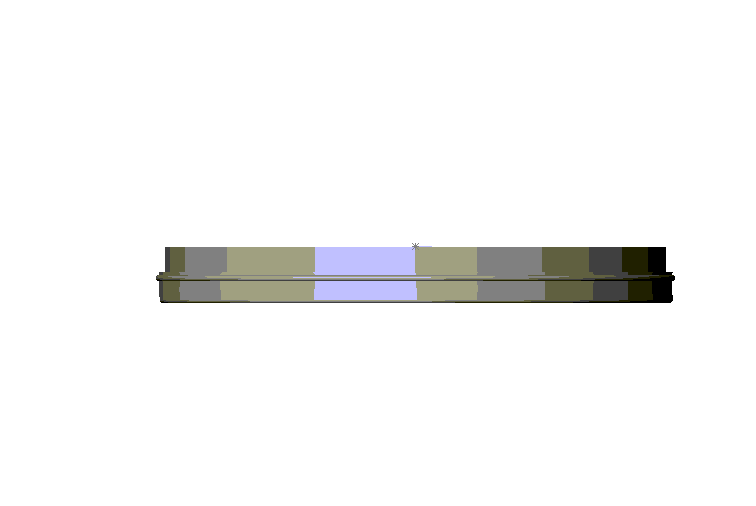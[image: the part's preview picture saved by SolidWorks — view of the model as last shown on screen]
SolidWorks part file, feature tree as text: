
SOLIDWORKS PART (.sldprt)
format: sldprt  version: not decoded by parser v0  size: 181,760 bytes
history: native  units: mm
features: sketch x6, cut_extrude x4, plane x3, extrude x1, chamfer x1, fillet x1, revolve x1 + 1 further entry (+6 scaffold rows collapsed)
feature tree (24):
  scaffold x6  (default folders/planes/origin — collapsed)
  "Corps de surface"
  plane  "Plan1"
  plane  "Plan2"
  plane  "Plan3"
  sketch  "Esquisse1"  dims[D1=82.0mm D2=35.0mm]
  extrude  "Base-Extrusion"  Depth=9mm
  sketch  "Esquisse2"  dims[D1=78.0mm D2=72.0mm]
  cut_extrude  "Enlèv. mat.-Extru.1"  Depth=2mm
  sketch  "Esquisse3"  dims[D1=40.0mm]
  cut_extrude  "Enlèv. mat.-Extru.2"  Depth=8mm
  chamfer  "Chanfrein1"  Distance=4mm
  fillet  "Congé1"  Radius=0.5mm
  sketch  "Esquisse4"  dims[D1=100.0mm D2=80.0mm]
  cut_extrude  "Enlèv. mat.-Extru.3"  Depth=4mm
  sketch  "Esquisse5"  dims[D1=52.0mm]
  cut_extrude  "Enlèv. mat.-Extru.4"  Depth=0.5mm
  sketch  "Esquisse6"  dims[D1=1.0mm D2=41.0mm D3=4.0mm]
  revolve  "Boss.-Révol.1"  Angle=360deg
decode coverage: 14 of 14 modeling features carry decoded parameters; 1 rows unclassified (native names shown)
note: suppression state not decoded; provenance and decode notes live in map.json
